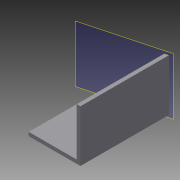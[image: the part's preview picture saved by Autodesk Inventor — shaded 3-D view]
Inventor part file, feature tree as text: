
AUTODESK INVENTOR PART (.ipt)
format: ipt  version: 2014 SP1 (Build 180222100, 222)  size: 76,800 bytes
history: native  units: in
note: dims shown in document units (in); Inventor stores cm internally (conversion verified against a paired STEP export)
features: extrude x1, plane x1, split x1, sketch x1
ambient origin geometry x8: Origin, YZ Plane, XZ Plane, XY Plane, X Axis, Y Axis, Z Axis, Center Point
bodies: Solid1 (feature_tree)
feature tree (4):
  extrude  "Extrusion1"  Depth=1.75in
  plane  "Work Plane1"
  split  "Split1"
  sketch  "Sketch1"  dims[d0=1.75in d1=1.75in d2=0.125in d3=3.0in d4=0.0in d5=15.0deg]
